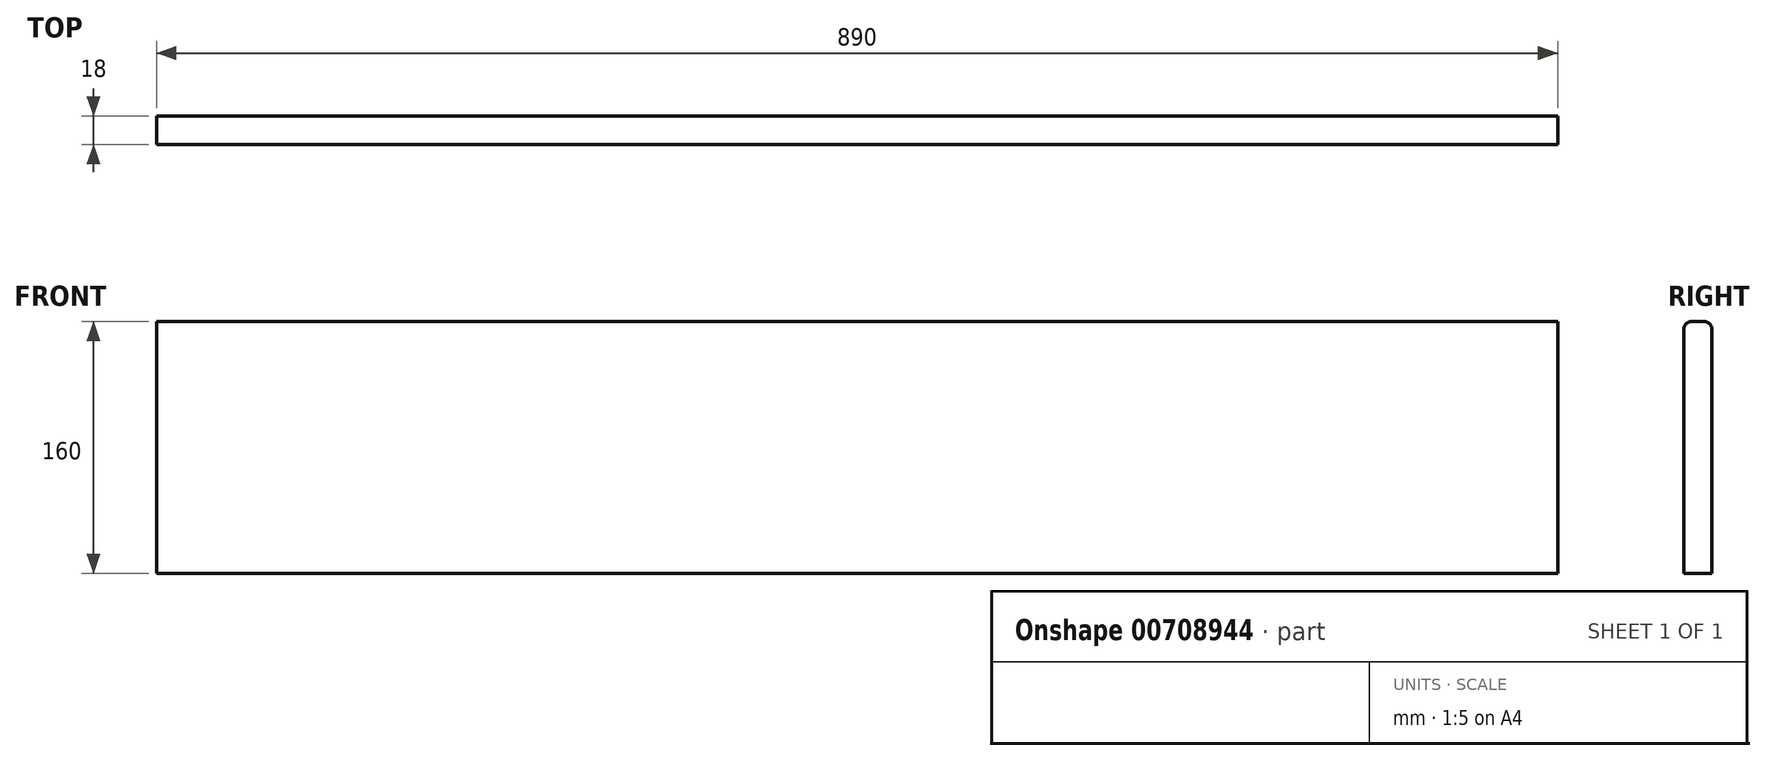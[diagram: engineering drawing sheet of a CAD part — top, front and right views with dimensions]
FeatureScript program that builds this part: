
annotation { "Feature Type Name" : "Feature", "Feature Type Description" : "" }
export const myFeature = defineFeature(function(context is Context, id is Id, definition is map)
    precondition{}
    {
        {
            var Q0;
            Q0=qCreatedBy(makeId("Front.planeOp"),FACE);
            var sketch = newSketch(context, id + "F0", { "sketchPlane" : qUnion([Q0])});
            skLineSegment(sketch, "E0.bottom", {"start": v(0, 0) * mm, "end": v(890, 0) * mm});
            skLineSegment(sketch, "E0.top", {"start": v(0, 160) * mm, "end": v(890, 160) * mm});
            skLineSegment(sketch, "E0.left", {"start": v(0, 0) * mm, "end": v(0, 160) * mm});
            skLineSegment(sketch, "E0.right", {"start": v(890, 0) * mm, "end": v(890, 160) * mm});
            skSolve(sketch);
        }
        {
            var Q0;
            Q0 = qSketchRegion(id + "F0", true);
            extrude(context, id + "F1", {"entities" : qUnion([Q0]), "depth" : 18 * mm, "offsetDistance" : 25 * mm});
        }
        {
            var Q0;
            Q0=makeQuery(id+"F1.opExtrude","CAP_EDGE",EDGE,{"disambiguationData":[OSD([sQuery(id+"F0.wireOp",EDGE,"E0.top")])],"isStart":false});
            var Q1;
            Q1=makeQuery(id+"F1.opExtrude","CAP_EDGE",EDGE,{"disambiguationData":[OSD([sQuery(id+"F0.wireOp",EDGE,"E0.top")])],"isStart":true});
            fillet(context, id + "F2", {"entities" : qUnion([Q0, Q1]), "radius" : 5 * mm, "tangentPropagation" : true, "allowEdgeOverflow" : false});
        }
    });
